# Revit family: MR_ОсветительныйПрибор_Stripled
name_source: partatom
category: Осветительные приборы
units: mm (PartAtom-declared; Revit-internal decimal feet)

## family parameters
Всегда вертикально = Нет
Источник света = Да
На основе рабочей плоскости = Да
Общий = Да
При загрузке вырезать с полостями = Нет
Размер круглого соединителя = Использовать диаметр
Тип детали = Нормальный
Точка расчета площади = Нет

## types (6) — shared parameters
ADSK_URL страницы изделия = https://martinirus.ru
ADSK_Группирование = Внутреннее освещение_светильник
ADSK_Единица измерения = шт.
ADSK_Завод-изготовитель = MartiniRUS
ADSK_Классификация нагрузок = Освещение
ADSK_Количество = 1
ADSK_Количество фаз = 1
ADSK_Количество фаз числовое = 1
ADSK_Коэффициент мощности = 0.98
ADSK_Материал = <По категории>
ADSK_Напряжение = 24 В
IP Class = IP65
Видимая форма излучения при визуализации = Да
Группа модели = Stripled
Излучение по длине прямоугольника = 10 мм
Класс Защиты = III
Описание = Stripled
Отметка по умолчанию = 1219 мм
Самосветящий материал = Источник света по умолчанию
Светофильтр = 16777215
Смещение цветовой температуры при затухании лампы = <Нет>
Угол наклона = 90.00°
zero-valued in all types: ADSK_Масса

## per-type parameters (varying)
| type | ADSK_Код изделия | ADSK_Номинальная мощность | ADSK_Полная мощность | ADSK_Размер_Длина | ADSK_Ток | Излучение по ширине прямоугольника | Полная установленная мощность | Файл фотометрической сетки |
| Stripled_High-flux_1000mm_3000k | P3139000WW(1000mm) | 15 Вт | 15 В·А | 1000 мм | 1 А | 1000 мм | 15 В·А | P3139000WW1000mm.ies |
| Stripled_High-flux_500mm_3000k | P3139000WW(500mm) | 8 Вт | 8 В·А | 500 мм | 0 А | 500 мм | 8 В·А | P3139000WW500mm.ies |
| Stripled_High-flux_100mm_3000k | P3139000WW(100mm) | 2 Вт | 2 В·А | 100 мм | 0 А | 100 мм | 2 В·А | P3139000WW100mm.ies |
| Stripled_Low-flux_1000mm_3000k | P3139100WW(1000mm) | 5 Вт | 5 В·А | 1000 мм | 0 А | 1000 мм | 5 В·А | P3139100WW1000mm.ies |
| Stripled_Low-flux_500mm_3000k | P3139100WW(500mm) | 3 Вт | 3 В·А | 500 мм | 0 А | 500 мм | 3 В·А | P3139100WW500mm.ies |
| Stripled_Low-flux_100mm_3000k | P3139100WW(100mm) | 1 Вт | 1 В·А | 100 мм | 0 А | 100 мм | 1 В·А | P3139100WW100mm.ies |

note: column(s) folded — value = type name in every type: ADSK_Наименование
